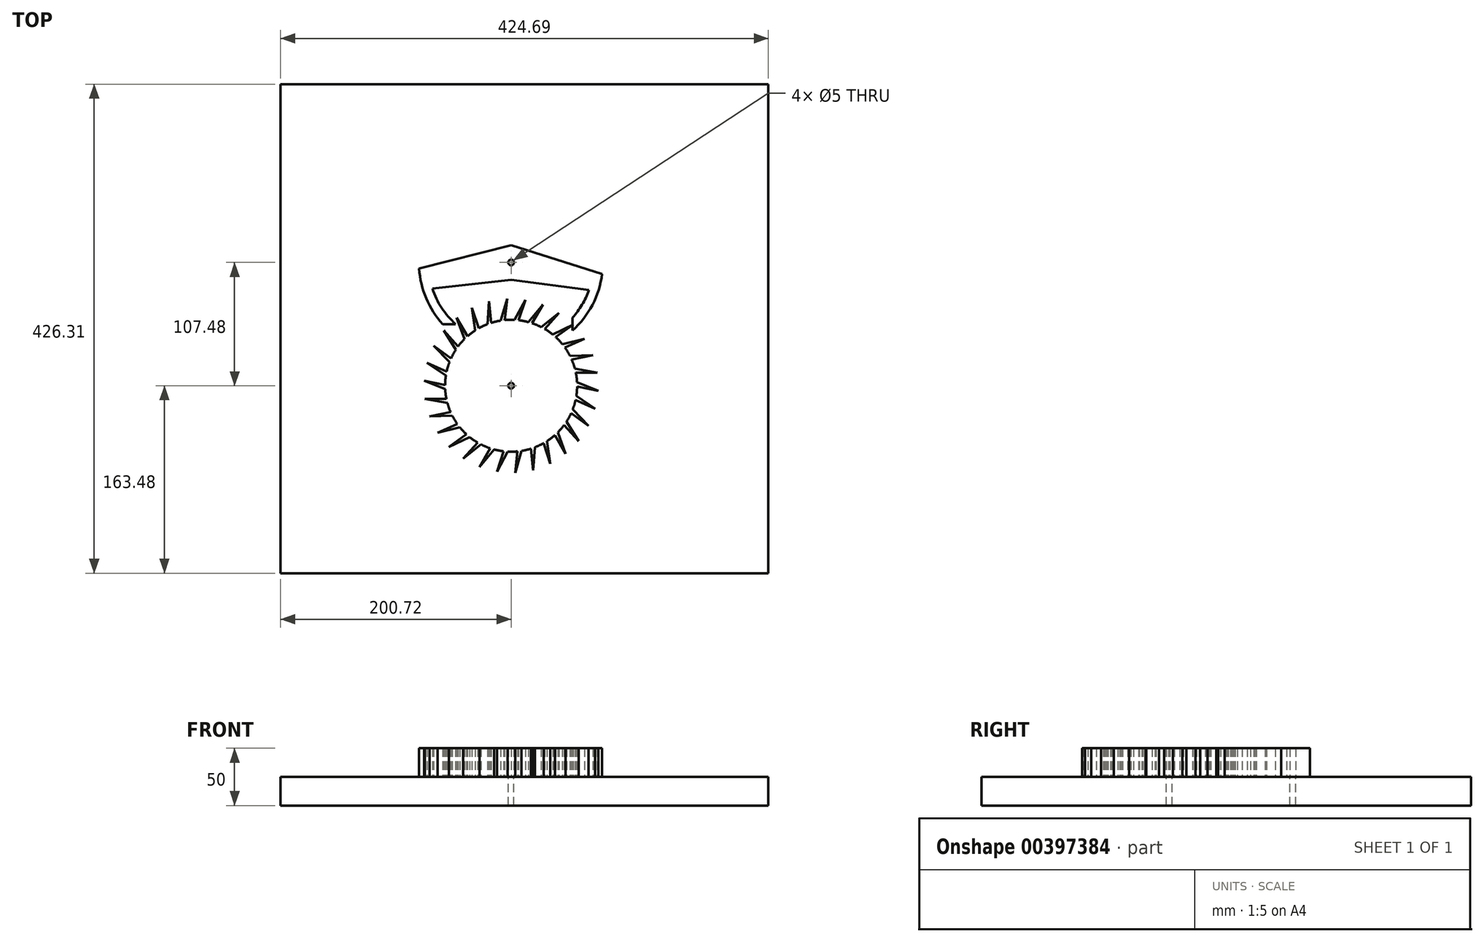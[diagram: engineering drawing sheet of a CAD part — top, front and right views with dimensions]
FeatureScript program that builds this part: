
annotation { "Feature Type Name" : "Feature", "Feature Type Description" : "" }
export const myFeature = defineFeature(function(context is Context, id is Id, definition is map)
    precondition{}
    {
        {
            var Q0;
            Q0=qCreatedBy(makeId("Top.planeOp"),FACE);
            var sketch = newSketch(context, id + "F0", { "sketchPlane" : qUnion([Q0])});
            skArc(sketch, "E0", {"start": v(-57.42, -3) * mm, "mid": v(-57.04, -7.24) * mm, "end": v(-56.35, -11.43) * mm});
            skCircle(sketch, "E1", {"center": v(0, 0) * mm, "radius": 160 * mm, "construction": true});
            skCircle(sketch, "E2", {"center": v(0, 0) * mm, "radius": 76 * mm, "construction": true});
            skLineSegment(sketch, "E3", {"start": v(0, 0) * mm, "end": v(-160.02, 160.02) * mm, "construction": true});
            skLineSegment(sketch, "E4", {"start": v(-40.66, 40.66) * mm, "end": v(-47.46, 59.36) * mm});
            skLineSegment(sketch, "E5", {"start": v(-38.07, 43.09) * mm, "end": v(-47.46, 59.36) * mm});
            skLineSegment(sketch, "E6.1.0", {"start": v(-46.2, 34.23) * mm, "end": v(-58.77, 48.2) * mm});
            skLineSegment(sketch, "E6.1.1", {"start": v(-48.22, 31.32) * mm, "end": v(-58.77, 48.2) * mm});
            skLineSegment(sketch, "E6.2.0", {"start": v(-52.3, 23.88) * mm, "end": v(-67.5, 34.92) * mm});
            skLineSegment(sketch, "E6.2.1", {"start": v(-53.68, 20.6) * mm, "end": v(-67.5, 34.92) * mm});
            skLineSegment(sketch, "E6.3.0", {"start": v(-56.13, 12.48) * mm, "end": v(-73.29, 20.12) * mm});
            skLineSegment(sketch, "E6.3.1", {"start": v(-56.8, 9) * mm, "end": v(-73.29, 20.12) * mm});
            skLineSegment(sketch, "E6.4.0", {"start": v(-57.5, 0.54) * mm, "end": v(-75.87, 4.44) * mm});
            skLineSegment(sketch, "E6.4.1", {"start": v(-57.42, -3) * mm, "end": v(-75.87, 4.44) * mm});
            skLineSegment(sketch, "E6.5.0", {"start": v(-56.35, -11.43) * mm, "end": v(-75.14, -11.43) * mm});
            skLineSegment(sketch, "E6.5.1", {"start": v(-55.54, -14.88) * mm, "end": v(-75.14, -11.43) * mm});
            skLineSegment(sketch, "E6.6.0", {"start": v(-52.75, -22.9) * mm, "end": v(-71.12, -26.8) * mm});
            skLineSegment(sketch, "E6.6.1", {"start": v(-51.23, -26.1) * mm, "end": v(-71.12, -26.8) * mm});
            skLineSegment(sketch, "E6.7.0", {"start": v(-46.83, -33.36) * mm, "end": v(-64, -41) * mm});
            skLineSegment(sketch, "E6.7.1", {"start": v(-44.69, -36.19) * mm, "end": v(-64, -41) * mm});
            skLineSegment(sketch, "E6.8.0", {"start": v(-38.87, -42.37) * mm, "end": v(-54.07, -53.4) * mm});
            skLineSegment(sketch, "E6.8.1", {"start": v(-36.19, -44.69) * mm, "end": v(-54.07, -53.4) * mm});
            skLineSegment(sketch, "E6.9.0", {"start": v(-29.22, -49.52) * mm, "end": v(-41.78, -63.48) * mm});
            skLineSegment(sketch, "E6.9.1", {"start": v(-26.1, -51.23) * mm, "end": v(-41.78, -63.48) * mm});
            skLineSegment(sketch, "E6.10.0", {"start": v(-18.28, -54.52) * mm, "end": v(-27.67, -70.78) * mm});
            skLineSegment(sketch, "E6.10.1", {"start": v(-14.88, -55.54) * mm, "end": v(-27.67, -70.78) * mm});
            skLineSegment(sketch, "E6.11.0", {"start": v(-6.55, -57.13) * mm, "end": v(-12.35, -74.99) * mm});
            skLineSegment(sketch, "E6.11.1", {"start": v(-3, -57.42) * mm, "end": v(-12.35, -74.99) * mm});
            skLineSegment(sketch, "E6.12.0", {"start": v(5.47, -57.24) * mm, "end": v(3.51, -75.92) * mm});
            skLineSegment(sketch, "E6.12.1", {"start": v(9, -56.8) * mm, "end": v(3.51, -75.92) * mm});
            skLineSegment(sketch, "E6.13.0", {"start": v(17.25, -54.85) * mm, "end": v(19.22, -73.53) * mm});
            skLineSegment(sketch, "E6.13.1", {"start": v(20.6, -53.68) * mm, "end": v(19.22, -73.53) * mm});
            skLineSegment(sketch, "E6.14.0", {"start": v(28.28, -50.06) * mm, "end": v(34.09, -67.93) * mm});
            skLineSegment(sketch, "E6.14.1", {"start": v(31.32, -48.22) * mm, "end": v(34.09, -67.93) * mm});
            skLineSegment(sketch, "E6.15.0", {"start": v(38.07, -43.09) * mm, "end": v(47.46, -59.36) * mm});
            skLineSegment(sketch, "E6.15.1", {"start": v(40.66, -40.66) * mm, "end": v(47.46, -59.36) * mm});
            skLineSegment(sketch, "E6.16.0", {"start": v(46.2, -34.23) * mm, "end": v(58.77, -48.2) * mm});
            skLineSegment(sketch, "E6.16.1", {"start": v(48.22, -31.32) * mm, "end": v(58.77, -48.2) * mm});
            skLineSegment(sketch, "E6.17.0", {"start": v(52.3, -23.88) * mm, "end": v(67.5, -34.92) * mm});
            skLineSegment(sketch, "E6.17.1", {"start": v(53.68, -20.6) * mm, "end": v(67.5, -34.92) * mm});
            skLineSegment(sketch, "E6.18.0", {"start": v(56.13, -12.48) * mm, "end": v(73.29, -20.12) * mm});
            skLineSegment(sketch, "E6.18.1", {"start": v(56.8, -9) * mm, "end": v(73.29, -20.12) * mm});
            skLineSegment(sketch, "E6.19.0", {"start": v(57.5, -0.54) * mm, "end": v(75.87, -4.44) * mm});
            skLineSegment(sketch, "E6.19.1", {"start": v(57.42, 3) * mm, "end": v(75.87, -4.44) * mm});
            skLineSegment(sketch, "E6.20.0", {"start": v(56.35, 11.43) * mm, "end": v(75.14, 11.43) * mm});
            skLineSegment(sketch, "E6.20.1", {"start": v(55.54, 14.88) * mm, "end": v(75.14, 11.43) * mm});
            skLineSegment(sketch, "E6.21.0", {"start": v(52.75, 22.9) * mm, "end": v(71.12, 26.8) * mm});
            skLineSegment(sketch, "E6.21.1", {"start": v(51.23, 26.1) * mm, "end": v(71.12, 26.8) * mm});
            skLineSegment(sketch, "E6.22.0", {"start": v(46.83, 33.36) * mm, "end": v(64, 41) * mm});
            skLineSegment(sketch, "E6.22.1", {"start": v(44.69, 36.19) * mm, "end": v(64, 41) * mm});
            skLineSegment(sketch, "E6.23.0", {"start": v(38.87, 42.37) * mm, "end": v(54.07, 53.4) * mm});
            skLineSegment(sketch, "E6.23.1", {"start": v(36.19, 44.69) * mm, "end": v(54.07, 53.4) * mm});
            skLineSegment(sketch, "E6.24.0", {"start": v(29.22, 49.52) * mm, "end": v(41.78, 63.48) * mm});
            skLineSegment(sketch, "E6.24.1", {"start": v(26.1, 51.23) * mm, "end": v(41.78, 63.48) * mm});
            skLineSegment(sketch, "E6.25.0", {"start": v(18.28, 54.52) * mm, "end": v(27.67, 70.78) * mm});
            skLineSegment(sketch, "E6.25.1", {"start": v(14.88, 55.54) * mm, "end": v(27.67, 70.78) * mm});
            skLineSegment(sketch, "E6.26.0", {"start": v(6.55, 57.13) * mm, "end": v(12.35, 74.99) * mm});
            skLineSegment(sketch, "E6.26.1", {"start": v(3, 57.42) * mm, "end": v(12.35, 74.99) * mm});
            skLineSegment(sketch, "E6.27.0", {"start": v(-5.47, 57.24) * mm, "end": v(-3.51, 75.92) * mm});
            skLineSegment(sketch, "E6.27.1", {"start": v(-9, 56.8) * mm, "end": v(-3.51, 75.92) * mm});
            skLineSegment(sketch, "E6.28.0", {"start": v(-17.25, 54.85) * mm, "end": v(-19.22, 73.53) * mm});
            skLineSegment(sketch, "E6.28.1", {"start": v(-20.6, 53.68) * mm, "end": v(-19.22, 73.53) * mm});
            skLineSegment(sketch, "E6.29.0", {"start": v(-28.28, 50.06) * mm, "end": v(-34.09, 67.93) * mm});
            skLineSegment(sketch, "E6.29.1", {"start": v(-31.32, 48.22) * mm, "end": v(-34.09, 67.93) * mm});
            skArc(sketch, "E7.trimOffspring", {"start": v(-55.54, -14.88) * mm, "mid": v(-54.3, -18.94) * mm, "end": v(-52.75, -22.9) * mm});
            skArc(sketch, "E8.trimOffspring", {"start": v(-51.23, -26.1) * mm, "mid": v(-49.17, -29.81) * mm, "end": v(-46.83, -33.36) * mm});
            skArc(sketch, "E9.trimOffspring", {"start": v(-56.8, 9) * mm, "mid": v(-57.3, 4.78) * mm, "end": v(-57.5, 0.54) * mm});
            skArc(sketch, "E10.trimOffspring", {"start": v(-53.68, 20.6) * mm, "mid": v(-55.05, 16.59) * mm, "end": v(-56.13, 12.48) * mm});
            skArc(sketch, "E11.trimOffspring", {"start": v(-48.22, 31.32) * mm, "mid": v(-50.4, 27.67) * mm, "end": v(-52.3, 23.88) * mm});
            skArc(sketch, "E12.trimOffspring", {"start": v(-40.66, 40.66) * mm, "mid": v(-43.55, 37.55) * mm, "end": v(-46.2, 34.23) * mm});
            skArc(sketch, "E13.trimOffspring", {"start": v(-31.32, 48.22) * mm, "mid": v(-34.79, 45.78) * mm, "end": v(-38.07, 43.09) * mm});
            skArc(sketch, "E14.trimOffspring", {"start": v(-20.6, 53.68) * mm, "mid": v(-24.51, 52.01) * mm, "end": v(-28.28, 50.06) * mm});
            skArc(sketch, "E15.trimOffspring", {"start": v(-9, 56.8) * mm, "mid": v(-13.16, 55.97) * mm, "end": v(-17.25, 54.85) * mm});
            skArc(sketch, "E16.trimOffspring", {"start": v(3, 57.42) * mm, "mid": v(-1.24, 57.49) * mm, "end": v(-5.47, 57.24) * mm});
            skArc(sketch, "E17.trimOffspring", {"start": v(14.88, 55.54) * mm, "mid": v(10.74, 56.49) * mm, "end": v(6.55, 57.13) * mm});
            skArc(sketch, "E18.trimOffspring", {"start": v(26.1, 51.23) * mm, "mid": v(22.25, 53.02) * mm, "end": v(18.28, 54.52) * mm});
            skArc(sketch, "E19.trimOffspring", {"start": v(36.19, 44.69) * mm, "mid": v(32.8, 47.23) * mm, "end": v(29.22, 49.52) * mm});
            skArc(sketch, "E20.trimOffspring", {"start": v(44.69, 36.19) * mm, "mid": v(41.9, 39.38) * mm, "end": v(38.87, 42.37) * mm});
            skArc(sketch, "E21.trimOffspring", {"start": v(51.23, 26.1) * mm, "mid": v(49.17, 29.81) * mm, "end": v(46.83, 33.36) * mm});
            skArc(sketch, "E22.trimOffspring", {"start": v(55.54, 14.88) * mm, "mid": v(54.3, 18.94) * mm, "end": v(52.75, 22.9) * mm});
            skArc(sketch, "E23.trimOffspring", {"start": v(57.42, 3) * mm, "mid": v(57.04, 7.24) * mm, "end": v(56.35, 11.43) * mm});
            skArc(sketch, "E24.trimOffspring", {"start": v(56.8, -9) * mm, "mid": v(57.3, -4.78) * mm, "end": v(57.5, -0.54) * mm});
            skArc(sketch, "E25.trimOffspring", {"start": v(53.68, -20.6) * mm, "mid": v(55.05, -16.59) * mm, "end": v(56.13, -12.48) * mm});
            skArc(sketch, "E26.trimOffspring", {"start": v(48.22, -31.32) * mm, "mid": v(50.4, -27.67) * mm, "end": v(52.3, -23.88) * mm});
            skArc(sketch, "E27.trimOffspring", {"start": v(40.66, -40.66) * mm, "mid": v(43.55, -37.55) * mm, "end": v(46.2, -34.23) * mm});
            skArc(sketch, "E28.trimOffspring", {"start": v(31.32, -48.22) * mm, "mid": v(34.79, -45.78) * mm, "end": v(38.07, -43.09) * mm});
            skArc(sketch, "E29.trimOffspring", {"start": v(20.6, -53.68) * mm, "mid": v(24.51, -52.01) * mm, "end": v(28.28, -50.06) * mm});
            skArc(sketch, "E30.trimOffspring", {"start": v(9, -56.8) * mm, "mid": v(13.16, -55.97) * mm, "end": v(17.25, -54.85) * mm});
            skArc(sketch, "E31.trimOffspring", {"start": v(-3, -57.42) * mm, "mid": v(1.24, -57.49) * mm, "end": v(5.47, -57.24) * mm});
            skArc(sketch, "E32.trimOffspring", {"start": v(-14.88, -55.54) * mm, "mid": v(-10.74, -56.49) * mm, "end": v(-6.55, -57.13) * mm});
            skArc(sketch, "E33.trimOffspring", {"start": v(-26.1, -51.23) * mm, "mid": v(-22.25, -53.02) * mm, "end": v(-18.28, -54.52) * mm});
            skArc(sketch, "E34.trimOffspring", {"start": v(-36.19, -44.69) * mm, "mid": v(-32.8, -47.23) * mm, "end": v(-29.22, -49.52) * mm});
            skArc(sketch, "E35.trimOffspring", {"start": v(-44.69, -36.19) * mm, "mid": v(-41.9, -39.38) * mm, "end": v(-38.87, -42.37) * mm});
            skCircle(sketch, "E36", {"center": v(0, 0) * mm, "radius": 2.5 * mm});
            skLineSegment(sketch, "E37", {"start": v(0, 0) * mm, "end": v(6.55, 57.13) * mm, "construction": true});
            skLineSegment(sketch, "E38", {"start": v(0, 0) * mm, "end": v(18.28, 54.52) * mm, "construction": true});
            skLineSegment(sketch, "E39", {"start": v(0, 0) * mm, "end": v(120.8, 120.8) * mm, "construction": true});
            skSolve(sketch);
        }
        {
            var Q0;
            Q0 = qSketchRegion(id + "F0", true);
            extrude(context, id + "F1", {"entities" : qUnion([Q0]), "depth" : 25 * mm});
        }
        {
            var Q0;
            Q0=qCreatedBy(makeId("Top.planeOp"),FACE);
            var sketch = newSketch(context, id + "F2", { "sketchPlane" : qUnion([Q0])});
            skCircle(sketch, "E40", {"center": v(0, 0) * mm, "radius": 76 * mm, "construction": true});
            skPoint(sketch, "E41.0", {"position": v(19.22, -73.53) * mm});
            skLineSegment(sketch, "E42", {"start": v(0, 0) * mm, "end": v(-84.53, 84.53) * mm, "construction": true});
            skLineSegment(sketch, "E43", {"start": v(0, 0) * mm, "end": v(82.51, 82.51) * mm, "construction": true});
            skLineSegment(sketch, "E44", {"start": v(-53.74, 53.74) * mm, "end": v(0, 107.48) * mm, "construction": true});
            skLineSegment(sketch, "E45", {"start": v(0, 107.48) * mm, "end": v(53.74, 53.74) * mm, "construction": true});
            skLineSegment(sketch, "E46", {"start": v(0, 107.48) * mm, "end": v(-110.06, 8.38) * mm, "construction": true});
            skLineSegment(sketch, "E47", {"start": v(0, 107.48) * mm, "end": v(-99.1, -2.58) * mm, "construction": true});
            skLineSegment(sketch, "E48", {"start": v(0, 0) * mm, "end": v(-90.35, 81.35) * mm, "construction": true});
            skLineSegment(sketch, "E49", {"start": v(0, 0) * mm, "end": v(-81.35, 90.35) * mm, "construction": true});
            skLineSegment(sketch, "E50", {"start": v(0, 0) * mm, "end": v(85.16, 94.58) * mm, "construction": true});
            skLineSegment(sketch, "E51", {"start": v(0, 0) * mm, "end": v(94.58, 85.16) * mm, "construction": true});
            skLineSegment(sketch, "E52", {"start": v(0, 107.48) * mm, "end": v(94.92, 22.02) * mm, "construction": true});
            skLineSegment(sketch, "E53", {"start": v(0, 107.48) * mm, "end": v(85.46, 12.56) * mm, "construction": true});
            skArc(sketch, "E54", {"start": v(-59.68, 53.74) * mm, "mid": v(-73.98, 76.21) * mm, "end": v(-80.13, 102.12) * mm});
            skArc(sketch, "E55", {"start": v(-48.39, 53.74) * mm, "mid": v(-60.5, 67.86) * mm, "end": v(-68.6, 84.6) * mm});
            skArc(sketch, "E56", {"start": v(53.45, 48.12) * mm, "mid": v(70.8, 70.5) * mm, "end": v(79.25, 97.52) * mm});
            skArc(sketch, "E57", {"start": v(53.45, 59.36) * mm, "mid": v(61.77, 70.65) * mm, "end": v(67.75, 83.35) * mm});
            skLineSegment(sketch, "E58", {"start": v(-80.13, 102.12) * mm, "end": v(0, 122.48) * mm});
            skLineSegment(sketch, "E59", {"start": v(0, 122.48) * mm, "end": v(79.25, 97.52) * mm});
            skLineSegment(sketch, "E60", {"start": v(67.75, 83.35) * mm, "end": v(0, 92.48) * mm});
            skLineSegment(sketch, "E61", {"start": v(0, 92.48) * mm, "end": v(-68.6, 84.6) * mm});
            skCircle(sketch, "E62", {"center": v(0, 107.48) * mm, "radius": 15 * mm, "construction": true});
            skLineSegment(sketch, "E63", {"start": v(-59.68, 53.74) * mm, "end": v(-48.39, 53.74) * mm});
            skLineSegment(sketch, "E64", {"start": v(53.45, 48.12) * mm, "end": v(53.45, 59.36) * mm});
            skCircle(sketch, "E65", {"center": v(0, 107.48) * mm, "radius": 2.5 * mm});
            skSolve(sketch);
        }
        {
            var Q0;
            Q0 = qSketchRegion(id + "F2", true);
            extrude(context, id + "F3", {"entities" : qUnion([Q0]), "depth" : 25 * mm});
        }
        {
            var Q0;
            Q0=qCreatedBy(makeId("Top.planeOp"),FACE);
            var sketch = newSketch(context, id + "F4", { "sketchPlane" : qUnion([Q0])});
            skCircle(sketch, "E66.0", {"center": v(0, 0) * mm, "radius": 2.5 * mm});
            skLineSegment(sketch, "E67.bottom", {"start": v(-200.72, 262.83) * mm, "end": v(223.97, 262.83) * mm});
            skLineSegment(sketch, "E67.top", {"start": v(-200.72, -163.48) * mm, "end": v(223.97, -163.48) * mm});
            skLineSegment(sketch, "E67.left", {"start": v(-200.72, 262.83) * mm, "end": v(-200.72, -163.48) * mm});
            skLineSegment(sketch, "E67.right", {"start": v(223.97, 262.83) * mm, "end": v(223.97, -163.48) * mm});
            skCircle(sketch, "E68.0", {"center": v(0, 107.48) * mm, "radius": 2.5 * mm});
            skSolve(sketch);
        }
        {
            var Q0;
            Q0 = qSketchRegion(id + "F4", true);
            extrude(context, id + "F5", {"entities" : qUnion([Q0]), "oppositeDirection" : true, "depth" : 25 * mm});
        }
    });
